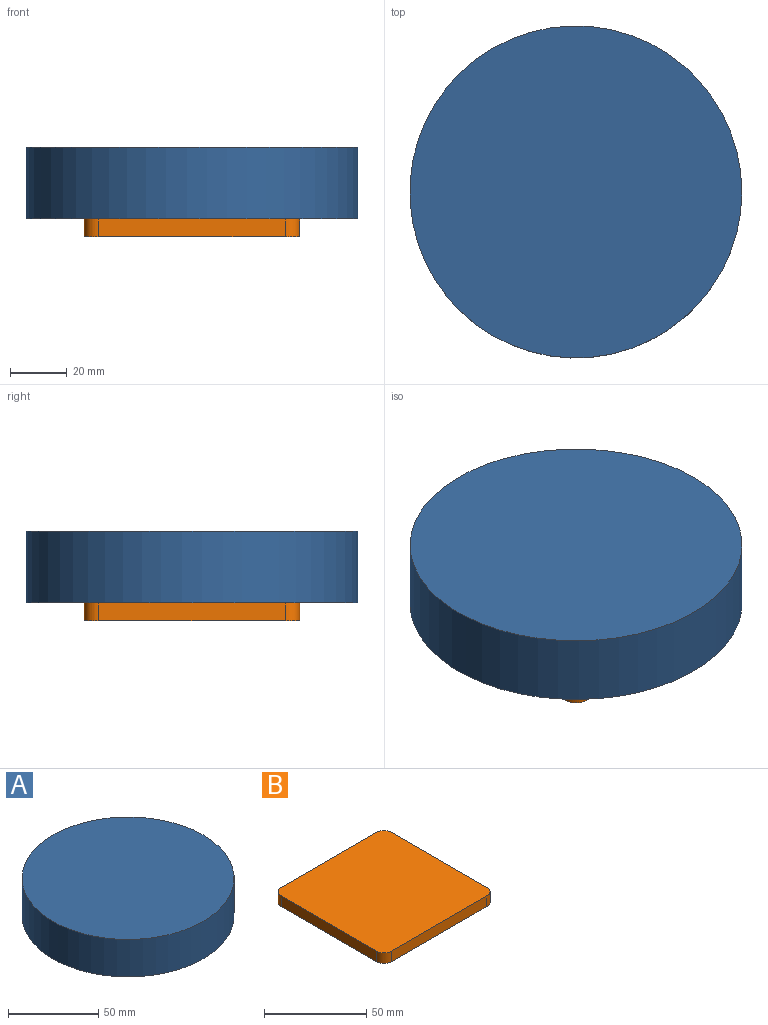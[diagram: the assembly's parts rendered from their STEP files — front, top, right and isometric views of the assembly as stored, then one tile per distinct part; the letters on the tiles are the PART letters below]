
ASSEMBLY  parts=2 mates=1
PART A: 3 faces, bbox 117.4x117.4x25.4 mm
  f0: cylinder r=58.72mm len=117.44mm, axis (0,0,-1), area 9371mm2, adj f1,f2
  f1: plane 117.44x117.44mm, normal (0,0,1), area 10831.5mm2, adj f0
  f2: plane 117.44x117.44mm, normal (0,0,-1), area 10831.5mm2, adj f0
PART B: 10 faces, bbox 76.2x76.2x6.4 mm
  f0: plane 66.04x6.35mm, normal (0,1,0), area 419.4mm2, adj f4,f5,f6,f9
  f1: plane 66.04x6.35mm, normal (-1,0,0), area 419.4mm2, adj f4,f5,f6,f7
  f2: plane 66.04x6.35mm, normal (0,-1,0), area 419.4mm2, adj f4,f5,f7,f8
  f3: plane 66.04x6.35mm, normal (1,0,0), area 419.4mm2, adj f4,f5,f8,f9
  f4: plane 76.2x76.2mm, normal (0,0,1), area 5784.3mm2, adj f0,f1,f2,f3,f6,f7,f8,f9
  f5: plane 76.2x76.2mm, normal (0,0,-1), area 5784.3mm2, adj f0,f1,f2,f3,f6,f7,f8,f9
  f6: cylinder r=5.08mm len=6.35mm, axis (0,0,-1), area 50.7mm2, adj f0,f1,f4,f5
  f7: cylinder r=5.08mm len=6.35mm, axis (0,0,1), area 50.7mm2, adj f1,f2,f4,f5
  f8: cylinder r=5.08mm len=6.35mm, axis (0,0,-1), area 50.7mm2, adj f2,f3,f4,f5
  f9: cylinder r=5.08mm len=6.35mm, axis (0,0,1), area 50.7mm2, adj f0,f3,f4,f5
PLACE A rot(axis=(1,0,0),180deg) t=(-103.78,-18.78,9.66)mm
PLACE B rot(axis=(1,0,0),180deg) t=(-103.78,-18.78,-15.74)mm
MATE fastened B.f5 <-> A.f0  axis (0,0,1) through (-103.78,-18.78,-15.74)mm
